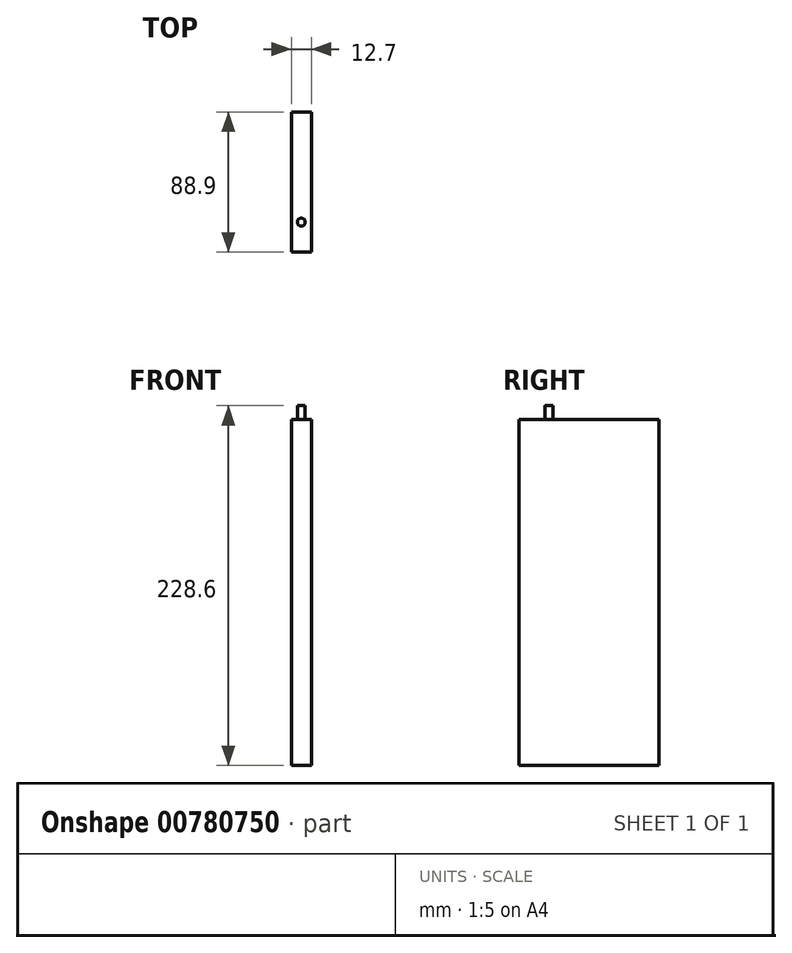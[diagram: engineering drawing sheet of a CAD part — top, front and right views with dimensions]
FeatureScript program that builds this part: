
annotation { "Feature Type Name" : "Feature", "Feature Type Description" : "" }
export const myFeature = defineFeature(function(context is Context, id is Id, definition is map)
    precondition{}
    {
        {
            var Q0;
            Q0=qCreatedBy(makeId("Right.planeOp"),FACE);
            var sketch = newSketch(context, id + "F0", { "sketchPlane" : qUnion([Q0])});
            skLineSegment(sketch, "E0.bottom", {"start": v(-36.4, 133.23) * mm, "end": v(52.5, 133.23) * mm});
            skLineSegment(sketch, "E0.top", {"start": v(-36.4, -86.48) * mm, "end": v(52.5, -86.48) * mm});
            skLineSegment(sketch, "E0.left", {"start": v(-36.4, 133.23) * mm, "end": v(-36.4, -86.48) * mm});
            skLineSegment(sketch, "E0.right", {"start": v(52.5, 133.23) * mm, "end": v(52.5, -86.48) * mm});
            skSolve(sketch);
        }
        {
            var Q0;
            Q0=makeQuery(id+"F0.imprint","IMPRINT",FACE,{"disambiguationData":[TD([[makeQuery(id+"F0.imprint","IMPRINT",EDGE,{"derivedFrom":sQuery(id+"F0.wireOp",EDGE,"E0.bottom")}),-1.0]])]});
            extrude(context, id + "F1", {"entities" : qUnion([Q0]), "depth" : 12.7 * mm, "offsetDistance" : 25.4 * mm});
        }
        {
            var Q0;
            Q0=makeQuery(id+"F1.opExtrude","SWEPT_FACE",FACE,{"disambiguationData":[OSD([sQuery(id+"F0.wireOp",EDGE,"E0.bottom")])]});
            var sketch = newSketch(context, id + "F2", { "sketchPlane" : qUnion([Q0])});
            skPoint(sketch, "E1", {"position": v(6.35, -36.4) * mm});
            skPoint(sketch, "E2", {"position": v(12.7, -17.35) * mm});
            skPoint(sketch, "E3", {"position": v(6.35, -17.35) * mm});
            skCircle(sketch, "E4", {"center": v(6.35, -17.35) * mm, "radius": 2.5 * mm});
            skSolve(sketch);
        }
        {
            var Q0;
            Q0=makeQuery(id+"F2.imprint","IMPRINT",FACE,{"disambiguationData":[TD([[makeQuery(id+"F2.imprint","IMPRINT",EDGE,{"derivedFrom":sQuery(id+"F2.wireOp",EDGE,"E4")}),1.0]])]});
            extrude(context, id + "F3", {"entities" : qUnion([Q0]), "operationType" : NewBodyOperationType.ADD, "depth" : 8.9 * mm, "offsetDistance" : 25.4 * mm});
        }
    });
